# Revit family: Sanitary_Waste-Bins_Slits_Paper-Bin_50L
name_source: partatom
category: Furniture
units: mm (PartAtom-declared; Revit-internal decimal feet)

## family parameters
Always vertical = No
Cut with Voids When Loaded = No
OmniClass Number = 23.40.20.00
OmniClass Title = General Furniture and Specialties
Room Calculation Point = No
Shared = No
Work Plane-Based = Yes

## types (1)
- Slits paper bin 50l
    AssetType = Fixed
    BIMObjectName = Sanitary_Waste-Bins_Slits_Paper-Bin_50L
    Brand = Svedholm
    Color = Various
    Cost = 0 $
    Default Elevation = 1219 mm
    Description = Paper Bin made of powder coated steel. All colours are available upon request. Adapted for bin liners 50 liters. The entire SLITS collection is approved by the Swedish BYGGVARUBEDÖMNINGEN and assessed in SundaHus Material Data.
    DurationUnit = Year
    IfcExportAs = IfcFurnishingElementType
    IfcExportType = MIRROR
    MainColor = White
    Manufacturer = Svedholm
    ManufacturerName = Svedholm
    ManufacturerURL = https://www.svedholm.se
    Material = Metal
    MirrorMainMaterial = RAL 7021
    Model = Slits paper bin 50l
    ModelNumber = 410.600.013
    NBSDescription = Mirrors
    NBSReference = 45-35-72/336
    Name = Slits_Paper-Bin_50L
    NominalDepth = 214 mm
    NominalHeight = 560 mm
    NominalLength = 262 mm
    ProductInformation = Paper Bin made of powder coated steel. All colours are available upon request. Adapted for bin liners 50 liters. The entire SLITS collection is approved by the Swedish BYGGVARUBEDÖMNINGEN and assessed in SundaHus Material Data.
    Shape = Sculptured
    Size = 560x262x214 mm
    URL = https://www.svedholm.se
    Uniclass2 = Pr_40_50_07_96
    Uniclass2015Description = Waste Bins
    Uniclass2015Reference = Pr_40_50_07_96
    Version = 1
    VersionDate = 06/07/2023
    WarrantyDurationUnit = Years

## geometry (parser evidence)
native form markers: Sweep x4
no freeform markers — native parametric forms only
